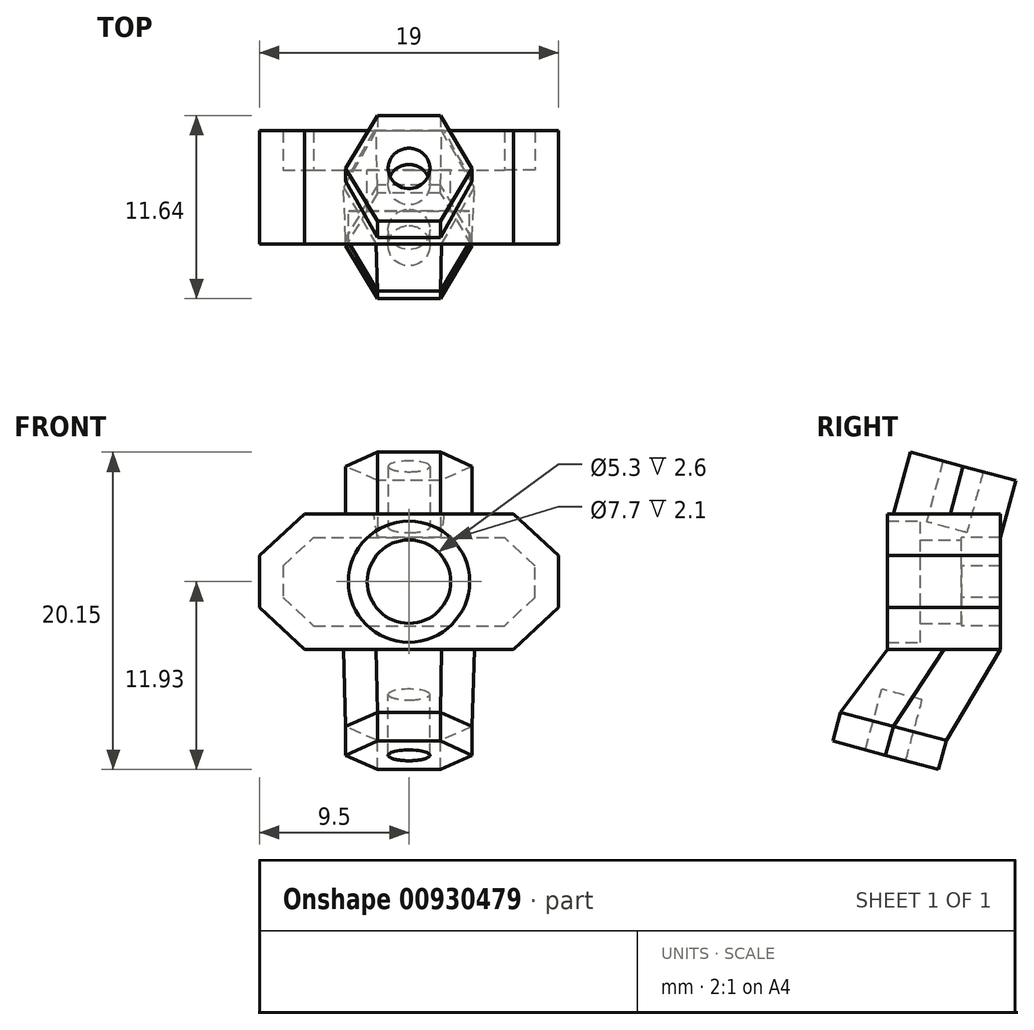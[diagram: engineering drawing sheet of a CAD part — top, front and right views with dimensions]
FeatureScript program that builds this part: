
annotation { "Feature Type Name" : "Feature", "Feature Type Description" : "" }
export const myFeature = defineFeature(function(context is Context, id is Id, definition is map)
    precondition{}
    {
        {
            var Q0;
            Q0=qCreatedBy(makeId("Front.planeOp"),FACE);
            var sketch = newSketch(context, id + "F0", { "sketchPlane" : qUnion([Q0])});
            skCircle(sketch, "E0", {"center": v(0, 0) * mm, "radius": 2.65 * mm});
            skLineSegment(sketch, "E1", {"start": v(0, 0) * mm, "end": v(0, 2.8) * mm, "construction": true});
            skLineSegment(sketch, "E2", {"start": v(0, 0) * mm, "end": v(0, -2.8) * mm, "construction": true});
            skLineSegment(sketch, "E3.bottom", {"start": v(-6.06, 2.8) * mm, "end": v(6.06, 2.8) * mm});
            skLineSegment(sketch, "E3.top", {"start": v(-6.06, -2.8) * mm, "end": v(6.06, -2.8) * mm});
            skLineSegment(sketch, "E4", {"start": v(0, 0) * mm, "end": v(-8, 0) * mm, "construction": true});
            skLineSegment(sketch, "E5", {"start": v(0, 0) * mm, "end": v(8, 0) * mm, "construction": true});
            skLineSegment(sketch, "E6", {"start": v(-8, 0) * mm, "end": v(-8, 1) * mm});
            skLineSegment(sketch, "E7", {"start": v(-8, 0) * mm, "end": v(-8, -1) * mm});
            skLineSegment(sketch, "E8.MirrorCS", {"start": v(8, 0) * mm, "end": v(8, 1) * mm});
            skLineSegment(sketch, "E9.MirrorCS", {"start": v(8, 0) * mm, "end": v(8, -1) * mm});
            skLineSegment(sketch, "E10", {"start": v(-8, 1) * mm, "end": v(-6.06, 2.8) * mm});
            skLineSegment(sketch, "E11", {"start": v(-8, -1) * mm, "end": v(-6.06, -2.8) * mm});
            skLineSegment(sketch, "E12.MirrorCS", {"start": v(8, 1) * mm, "end": v(6.06, 2.8) * mm});
            skLineSegment(sketch, "E13.MirrorCS", {"start": v(8, -1) * mm, "end": v(6.06, -2.8) * mm});
            skLineSegment(sketch, "E14.0", {"start": v(-9.5, 1.65) * mm, "end": v(-6.65, 4.3) * mm});
            skLineSegment(sketch, "E14.1", {"start": v(-9.5, 0) * mm, "end": v(-9.5, 1.65) * mm});
            skLineSegment(sketch, "E14.2", {"start": v(-6.65, 4.3) * mm, "end": v(6.65, 4.3) * mm});
            skLineSegment(sketch, "E14.3", {"start": v(-9.5, 0) * mm, "end": v(-9.5, -1.65) * mm});
            skLineSegment(sketch, "E14.4", {"start": v(-9.5, -1.65) * mm, "end": v(-6.65, -4.3) * mm});
            skLineSegment(sketch, "E14.5", {"start": v(-6.65, -4.3) * mm, "end": v(6.65, -4.3) * mm});
            skLineSegment(sketch, "E14.6", {"start": v(9.5, 1.65) * mm, "end": v(6.65, 4.3) * mm});
            skLineSegment(sketch, "E14.7", {"start": v(9.5, 0) * mm, "end": v(9.5, 1.65) * mm});
            skLineSegment(sketch, "E14.8", {"start": v(9.5, 0) * mm, "end": v(9.5, -1.65) * mm});
            skLineSegment(sketch, "E14.9", {"start": v(9.5, -1.65) * mm, "end": v(6.65, -4.3) * mm});
            skCircle(sketch, "E15", {"center": v(0, 0) * mm, "radius": 3.85 * mm});
            skCircle(sketch, "E16", {"center": v(0, 0) * mm, "radius": 4.5 * mm, "construction": true});
            skSolve(sketch);
        }
        {
            var Q0;
            Q0=makeQuery(id+"F0.imprint","IMPRINT",FACE,{"disambiguationData":[TD([[makeQuery(id+"F0.imprint","IMPRINT",EDGE,{"derivedFrom":sQuery(id+"F0.wireOp",EDGE,"E6")}),1.0]])]});
            var Q1;
            {var subQ0=sQuery(id+"F0.wireOp",EDGE,"E15");var subQ1=sQuery(id+"F0.wireOp",EDGE,"E3.top");var subQ2=makeQuery(id+"F0.imprint","INTERSECT",VERTEX,{"disambiguationData":[OD(0.0)],"derivedFrom":[subQ1,subQ0]});Q1=makeQuery(id+"F0.imprint","IMPRINT",FACE,{"disambiguationData":[TD([[makeQuery(id+"F0.imprint","IMPRINT",EDGE,{"disambiguationData":[TD([[subQ2,-1.0]])],"derivedFrom":subQ1}),-1.0]])]});}
            var Q2;
            {var subQ0=sQuery(id+"F0.wireOp",EDGE,"E15");var subQ1=sQuery(id+"F0.wireOp",EDGE,"E3.bottom");var subQ2=makeQuery(id+"F0.imprint","INTERSECT",VERTEX,{"disambiguationData":[OD(0.0)],"derivedFrom":[subQ1,subQ0]});Q2=makeQuery(id+"F0.imprint","IMPRINT",FACE,{"disambiguationData":[TD([[makeQuery(id+"F0.imprint","IMPRINT",EDGE,{"disambiguationData":[TD([[subQ2,-1.0]])],"derivedFrom":subQ1}),1.0]])]});}
            extrude(context, id + "F1", {"entities" : qUnion([Q0, Q1, Q2]), "oppositeDirection" : true, "depth" : 2.5 * mm, "offsetDistance" : 25 * mm});
        }
        {
            var Q0;
            Q0=makeQuery(id+"F0.imprint","IMPRINT",FACE,{"disambiguationData":[TD([[makeQuery(id+"F0.imprint","IMPRINT",EDGE,{"derivedFrom":sQuery(id+"F0.wireOp",EDGE,"E6")}),1.0]])]});
            var Q1;
            {var subQ0=sQuery(id+"F0.wireOp",EDGE,"E15");var subQ1=sQuery(id+"F0.wireOp",EDGE,"E3.bottom");var subQ2=makeQuery(id+"F0.imprint","INTERSECT",VERTEX,{"disambiguationData":[OD(0.0)],"derivedFrom":[subQ1,subQ0]});Q1=makeQuery(id+"F0.imprint","IMPRINT",FACE,{"disambiguationData":[TD([[makeQuery(id+"F0.imprint","IMPRINT",EDGE,{"disambiguationData":[TD([[subQ2,-1.0]])],"derivedFrom":subQ1}),1.0]])]});}
            var Q2;
            {var subQ0=sQuery(id+"F0.wireOp",EDGE,"E15");var subQ1=sQuery(id+"F0.wireOp",EDGE,"E3.top");var subQ2=makeQuery(id+"F0.imprint","INTERSECT",VERTEX,{"disambiguationData":[OD(0.0)],"derivedFrom":[subQ1,subQ0]});Q2=makeQuery(id+"F0.imprint","IMPRINT",FACE,{"disambiguationData":[TD([[makeQuery(id+"F0.imprint","IMPRINT",EDGE,{"disambiguationData":[TD([[subQ2,-1.0]])],"derivedFrom":subQ1}),-1.0]])]});}
            var Q3;
            Q3=makeQuery(id+"F0.imprint","IMPRINT",FACE,{"disambiguationData":[TD([[makeQuery(id+"F0.imprint","IMPRINT",EDGE,{"derivedFrom":sQuery(id+"F0.wireOp",EDGE,"E8.MirrorCS")}),1.0]])]});
            var Q4;
            Q4=makeQuery(id+"F0.imprint","IMPRINT",FACE,{"disambiguationData":[TD([[makeQuery(id+"F0.imprint","IMPRINT",EDGE,{"derivedFrom":sQuery(id+"F0.wireOp",EDGE,"E6")}),-1.0]])]});
            var Q5;
            Q5=makeQuery(id+"F0.imprint","IMPRINT",FACE,{"disambiguationData":[TD([[makeQuery(id+"F0.imprint","IMPRINT",EDGE,{"derivedFrom":sQuery(id+"F0.wireOp",EDGE,"E0")}),-1.0]])]});
            extrude(context, id + "F2", {"entities" : qUnion([Q0, Q1, Q2, Q3, Q4, Q5]), "operationType" : NewBodyOperationType.ADD, "depth" : 2.6 * mm, "offsetDistance" : 25 * mm});
        }
        {
            var Q0;
            Q0=makeQuery(id+"F0.imprint","IMPRINT",FACE,{"disambiguationData":[TD([[makeQuery(id+"F0.imprint","IMPRINT",EDGE,{"derivedFrom":sQuery(id+"F0.wireOp",EDGE,"E6")}),1.0]])]});
            var Q1;
            Q1=makeQuery(id+"F0.imprint","IMPRINT",FACE,{"disambiguationData":[TD([[makeQuery(id+"F0.imprint","IMPRINT",EDGE,{"derivedFrom":sQuery(id+"F0.wireOp",EDGE,"E6")}),-1.0]])]});
            var Q2;
            Q2=makeQuery(id+"F0.imprint","IMPRINT",FACE,{"disambiguationData":[TD([[makeQuery(id+"F0.imprint","IMPRINT",EDGE,{"derivedFrom":sQuery(id+"F0.wireOp",EDGE,"E8.MirrorCS")}),1.0]])]});
            extrude(context, id + "F3", {"entities" : qUnion([Q0, Q1, Q2]), "operationType" : NewBodyOperationType.ADD, "depth" : 4.7 * mm, "offsetDistance" : 25 * mm});
        }
        {
            var Q0;
            Q0=sQuery(id+"F0.wireOp",EDGE,"E5");
            cPlane(context, id + "F4", {"entities" : qUnion([Q0]), "cplaneType" : CPlaneType.LINE_ANGLE, "offset" : 25 * mm, "angle" : 255 * degree, "width" : 150 * mm, "height" : 150 * mm});
        }
        {
            var Q0;
            Q0=qCreatedBy(id+"F4.planeOp",FACE);
            var sketch = newSketch(context, id + "F5", { "sketchPlane" : qUnion([Q0])});
            skCircle(sketch, "E17.cCircle", {"center": v(0, 1.79) * mm, "radius": 3.48 * mm, "construction": true});
            skLineSegment(sketch, "E17.0", {"start": v(-2, 5.26) * mm, "end": v(2, 5.26) * mm});
            skLineSegment(sketch, "E17.1", {"start": v(2, 5.26) * mm, "end": v(4.02, 1.79) * mm});
            skLineSegment(sketch, "E17.2", {"start": v(4.02, 1.79) * mm, "end": v(2, -1.7) * mm});
            skLineSegment(sketch, "E17.3", {"start": v(2, -1.7) * mm, "end": v(-2, -1.7) * mm});
            skLineSegment(sketch, "E17.4", {"start": v(-2, -1.7) * mm, "end": v(-4.02, 1.79) * mm});
            skLineSegment(sketch, "E17.5", {"start": v(-4.02, 1.79) * mm, "end": v(-2, 5.26) * mm});
            skPoint(sketch, "E17.0.midPoint", {"position": v(0, 5.26) * mm});
            skCircle(sketch, "E18", {"center": v(0, 1.79) * mm, "radius": 1.32 * mm});
            skSolve(sketch);
        }
        {
            var Q0;
            Q0 = qSketchRegion(id + "F5", true);
            extrude(context, id + "F6", {"entities" : qUnion([Q0]), "oppositeDirection" : true, "depth" : 7.1 * mm, "offsetDistance" : 25 * mm, "hasSecondDirection" : true, "secondDirectionOppositeDirection" : true, "secondDirectionDepth" : 5 * mm});
        }
        {
            var Q0;
            Q0=makeQuery(id+"F5.imprint","IMPRINT",FACE,{"disambiguationData":[TD([[makeQuery(id+"F5.imprint","IMPRINT",EDGE,{"derivedFrom":sQuery(id+"F5.wireOp",EDGE,"E18")}),1.0]])]});
            extrude(context, id + "F7", {"entities" : qUnion([Q0]), "operationType" : NewBodyOperationType.REMOVE, "oppositeDirection" : true, "depth" : 7.1 * mm, "offsetDistance" : 25 * mm, "hasSecondDirection" : true, "secondDirectionOppositeDirection" : true, "secondDirectionDepth" : 3.1 * mm});
        }
        {
            var Q0;
            Q0=makeQuery(id+"F6.opExtrude","CAP_FACE",FACE,{"disambiguationData":[OSD([sQuery(id+"F5.wireOp",EDGE,"E17.0"),sQuery(id+"F5.wireOp",EDGE,"E17.1"),sQuery(id+"F5.wireOp",EDGE,"E17.2"),sQuery(id+"F5.wireOp",EDGE,"E17.3"),sQuery(id+"F5.wireOp",EDGE,"E17.4"),sQuery(id+"F5.wireOp",EDGE,"E17.5"),sQuery(id+"F5.wireOp",EDGE,"E18")])],"isStart":true});
            extrude(context, id + "F8", {"entities" : qUnion([Q0]), "operationType" : NewBodyOperationType.ADD, "endBound" : BoundingType.UP_TO_NEXT, "depth" : 25 * mm, "offsetDistance" : 25 * mm});
        }
        {
            var Q0;
            Q0 = qSketchRegion(id + "F5", true);
            var Q1;
            Q1=makeQuery(id+"F5.imprint","IMPRINT",FACE,{"disambiguationData":[TD([[makeQuery(id+"F5.imprint","IMPRINT",EDGE,{"derivedFrom":sQuery(id+"F5.wireOp",EDGE,"E18")}),1.0]])]});
            extrude(context, id + "F9", {"entities" : qUnion([Q0, Q1]), "depth" : 11.9 * mm, "offsetDistance" : 25 * mm, "hasSecondDirection" : true, "secondDirectionOppositeDirection" : false, "secondDirectionDepth" : 10 * mm});
        }
        {
            var Q0;
            {var subQ0=sQuery(id+"F0.wireOp",EDGE,"E14.5");Q0=makeQuery(id+"F3.boolean.opBoolean","MERGE",FACE,{"derivedFrom":[makeQuery(id+"F2.boolean.opBoolean","MERGE",FACE,{"derivedFrom":[makeQuery(id+"F1.opExtrude","SWEPT_FACE",FACE,{"disambiguationData":[OSD([subQ0])]}),makeQuery(id+"F2.opExtrude","SWEPT_FACE",FACE,{"disambiguationData":[OSD([subQ0])]})]}),makeQuery(id+"F3.opExtrude","SWEPT_FACE",FACE,{"disambiguationData":[OSD([subQ0])]})]});}
            var sketch = newSketch(context, id + "F10", { "sketchPlane" : qUnion([Q0])});
            skCircle(sketch, "E19.cCircle", {"center": v(0, 1.1) * mm, "radius": 3.6 * mm, "construction": true});
            skLineSegment(sketch, "E19.0", {"start": v(-2.08, 4.7) * mm, "end": v(2.08, 4.7) * mm});
            skLineSegment(sketch, "E19.1", {"start": v(2.08, 4.7) * mm, "end": v(4.16, 1.1) * mm});
            skLineSegment(sketch, "E19.2", {"start": v(4.16, 1.1) * mm, "end": v(2.08, -2.5) * mm});
            skLineSegment(sketch, "E19.3", {"start": v(2.08, -2.5) * mm, "end": v(-2.08, -2.5) * mm});
            skLineSegment(sketch, "E19.4", {"start": v(-2.08, -2.5) * mm, "end": v(-4.16, 1.1) * mm});
            skLineSegment(sketch, "E19.5", {"start": v(-4.16, 1.1) * mm, "end": v(-2.08, 4.7) * mm});
            skPoint(sketch, "E19.0.midPoint", {"position": v(0, 4.7) * mm});
            skSolve(sketch);
        }
        {
            var Q0;
            Q0=makeQuery(id+"F9.opExtrude","CAP_FACE",FACE,{"disambiguationData":[OSD([sQuery(id+"F5.wireOp",EDGE,"E17.0"),sQuery(id+"F5.wireOp",EDGE,"E17.1"),sQuery(id+"F5.wireOp",EDGE,"E17.2"),sQuery(id+"F5.wireOp",EDGE,"E17.3"),sQuery(id+"F5.wireOp",EDGE,"E17.4"),sQuery(id+"F5.wireOp",EDGE,"E17.5")])],"isStart":true});
            var Q1;
            Q1=makeQuery(id+"F10.imprint","IMPRINT",FACE,{"disambiguationData":[TD([[makeQuery(id+"F10.imprint","IMPRINT",EDGE,{"derivedFrom":sQuery(id+"F10.wireOp",EDGE,"E19.0")}),-1.0]])]});
            loft(context, id + "F11", {"operationType" : NewBodyOperationType.ADD, "sheetProfilesArray" : [{ "sheetProfileEntities" : qUnion([Q0]) }, { "sheetProfileEntities" : qUnion([Q1]) }]});
        }
        {
            var Q0;
            Q0=makeQuery(id+"F5.imprint","IMPRINT",FACE,{"disambiguationData":[TD([[makeQuery(id+"F5.imprint","IMPRINT",EDGE,{"derivedFrom":sQuery(id+"F5.wireOp",EDGE,"E18")}),1.0]])]});
            extrude(context, id + "F12", {"entities" : qUnion([Q0]), "operationType" : NewBodyOperationType.REMOVE, "depth" : 11.9 * mm, "offsetDistance" : 25 * mm, "hasSecondDirection" : true, "secondDirectionOppositeDirection" : false, "secondDirectionDepth" : 7.9 * mm});
        }
    });
